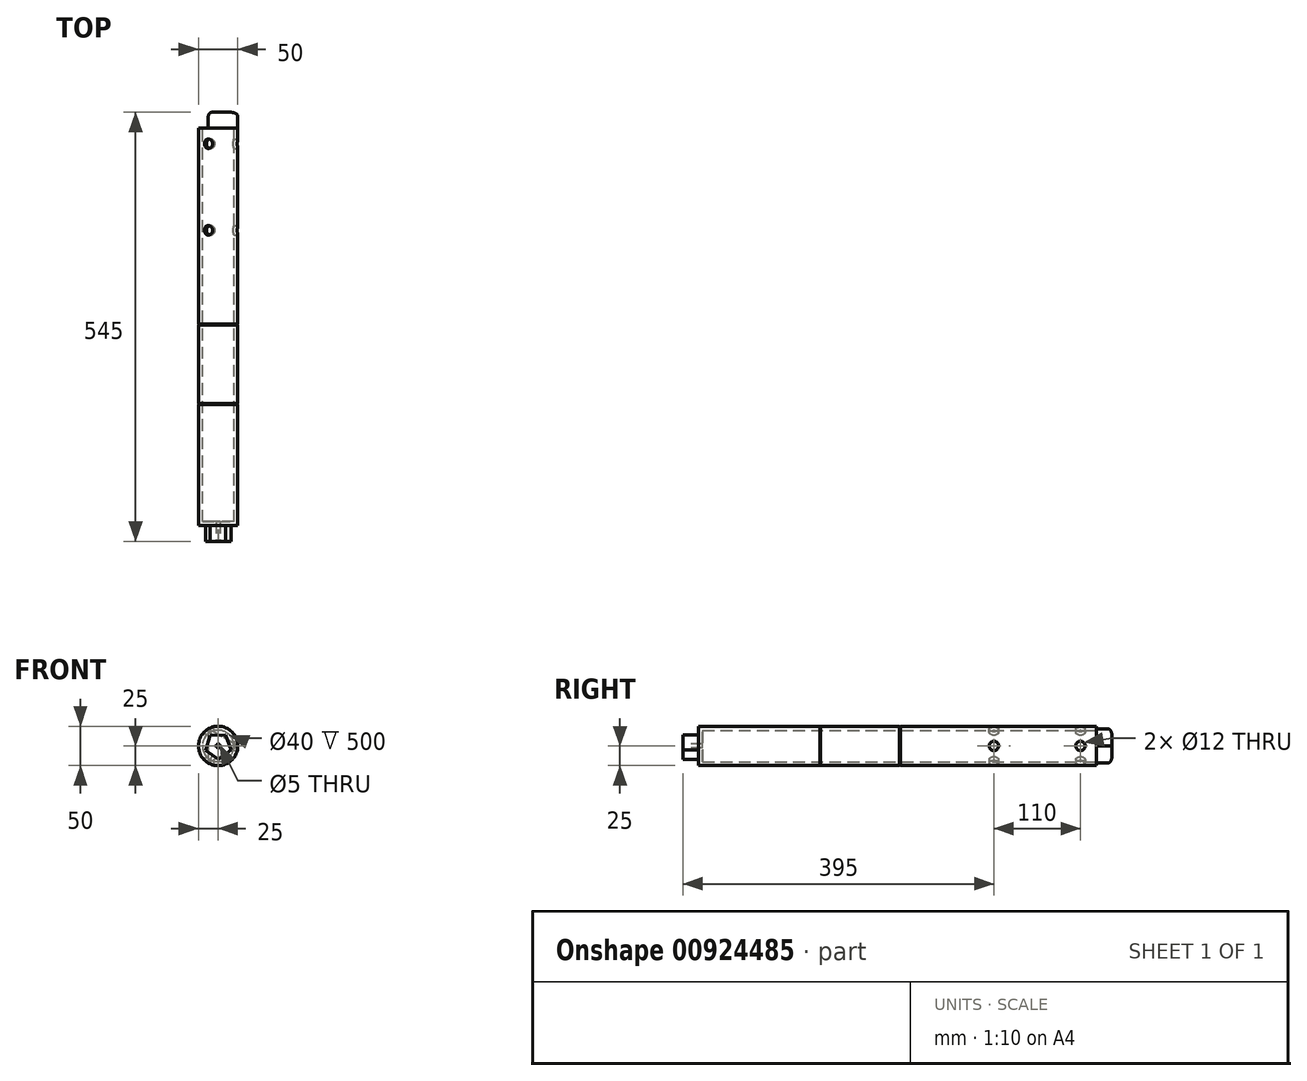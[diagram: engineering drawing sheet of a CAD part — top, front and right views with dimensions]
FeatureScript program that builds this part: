
annotation { "Feature Type Name" : "Feature", "Feature Type Description" : "" }
export const myFeature = defineFeature(function(context is Context, id is Id, definition is map)
    precondition{}
    {
        {
            var Q0;
            Q0=qCreatedBy(makeId("Front.planeOp"),FACE);
            var sketch = newSketch(context, id + "F0", { "sketchPlane" : qUnion([Q0])});
            skCircle(sketch, "E0", {"center": v(0, 0) * mm, "radius": 25 * mm});
            skCircle(sketch, "E1", {"center": v(0, 0) * mm, "radius": 20 * mm});
            skSolve(sketch);
        }
        {
            var Q0;
            Q0=makeQuery(id+"F0.imprint","IMPRINT",FACE,{"disambiguationData":[TD([[makeQuery(id+"F0.imprint","IMPRINT",EDGE,{"derivedFrom":sQuery(id+"F0.wireOp",EDGE,"E0")}),1.0]])]});
            extrude(context, id + "F1", {"entities" : qUnion([Q0]), "depth" : 500 * mm, "offsetDistance" : 25 * mm});
        }
        {
            var Q0;
            Q0=makeQuery(id+"F1.opExtrude","CAP_FACE",FACE,{"disambiguationData":[OSD([sQuery(id+"F0.wireOp",EDGE,"E0"),sQuery(id+"F0.wireOp",EDGE,"E1")])],"isStart":false});
            var sketch = newSketch(context, id + "F2", { "sketchPlane" : qUnion([Q0])});
            skCircle(sketch, "E2", {"center": v(0, 0) * mm, "radius": 25 * mm});
            skSolve(sketch);
        }
        {
            var Q0;
            Q0=qSketchRegion(id+"F2",true);
            extrude(context, id + "F3", {"entities" : qUnion([Q0]), "operationType" : NewBodyOperationType.ADD, "depth" : 5 * mm, "offsetDistance" : 25 * mm});
        }
        {
            var Q0;
            Q0=makeQuery(id+"F3.opExtrude","CAP_FACE",FACE,{"disambiguationData":[OSD([sQuery(id+"F2.wireOp",EDGE,"E2")])],"isStart":false});
            var sketch = newSketch(context, id + "F4", { "sketchPlane" : qUnion([Q0])});
            skCircle(sketch, "E3.cCircle", {"center": v(0, 0) * mm, "radius": 13.77 * mm, "construction": true});
            skLineSegment(sketch, "E3.0", {"start": v(0.38, -17.01) * mm, "end": v(-16.06, -5.62) * mm});
            skLineSegment(sketch, "E3.1", {"start": v(-16.06, -5.62) * mm, "end": v(-10.3, 13.54) * mm});
            skLineSegment(sketch, "E3.2", {"start": v(-10.3, 13.54) * mm, "end": v(9.7, 13.99) * mm});
            skLineSegment(sketch, "E3.3", {"start": v(9.7, 13.99) * mm, "end": v(16.3, -4.9) * mm});
            skLineSegment(sketch, "E3.4", {"start": v(16.3, -4.9) * mm, "end": v(0.38, -17.01) * mm});
            skPoint(sketch, "E3.0.midPoint", {"position": v(-7.84, -11.32) * mm});
            skSolve(sketch);
        }
        {
            var Q0;
            Q0=makeQuery(id+"F4.imprint","IMPRINT",FACE,{"disambiguationData":[TD([[makeQuery(id+"F4.imprint","IMPRINT",EDGE,{"derivedFrom":sQuery(id+"F4.wireOp",EDGE,"E3.0")}),-1.0]])]});
            extrude(context, id + "F5", {"entities" : qUnion([Q0]), "operationType" : NewBodyOperationType.ADD, "depth" : 20 * mm, "offsetDistance" : 25 * mm});
        }
        {
            var Q0;
            Q0=makeQuery(id+"F5.opExtrude","CAP_FACE",FACE,{"disambiguationData":[OSD([sQuery(id+"F4.wireOp",EDGE,"E3.0"),sQuery(id+"F4.wireOp",EDGE,"E3.1"),sQuery(id+"F4.wireOp",EDGE,"E3.2"),sQuery(id+"F4.wireOp",EDGE,"E3.3"),sQuery(id+"F4.wireOp",EDGE,"E3.4")])],"isStart":false});
            var sketch = newSketch(context, id + "F6", { "sketchPlane" : qUnion([Q0])});
            skPoint(sketch, "E4", {"position": v(0, 0) * mm});
            skSolve(sketch);
        }
        {
            var Q0;
            Q0=sQuery(id+"F6.wireOp",VERTEX,"E4");
            var Q1;
            Q1=makeQuery(id+"F1.opExtrude","SWEPT_BODY",BODY,{"disambiguationData":[OSD([sQuery(id+"F0.wireOp",EDGE,"E0"),sQuery(id+"F0.wireOp",EDGE,"E1")])]});
            hole(context, id + "F7", {"style" : HoleStyle.SIMPLE, "endStyle" : HoleEndStyle.THROUGH, "holeDiameter" : 5 * mm, "majorDiameter" : 5 * mm, "isTappedThrough" : true, "tappedDepth" : 12 * mm, "tapClearance" : 3, "locations" : qUnion([Q0]), "scope" : qUnion([Q1])});
        }
        {
            var Q0;
            Q0=qCreatedBy(makeId("Right.planeOp"),FACE);
            cPlane(context, id + "F8", {"entities" : qUnion([Q0]), "cplaneType" : CPlaneType.OFFSET, "offset" : 25 * mm, "width" : 150 * mm, "height" : 150 * mm});
        }
        {
            var Q0;
            Q0=qCreatedBy(id+"F8.planeOp",FACE);
            var sketch = newSketch(context, id + "F9", { "sketchPlane" : qUnion([Q0])});
            skPoint(sketch, "E5", {"position": v(-20, 0) * mm});
            skPoint(sketch, "E6", {"position": v(-130, 0) * mm});
            skSolve(sketch);
        }
        {
            var Q0;
            Q0=sQuery(id+"F9.wireOp",VERTEX,"E5");
            var Q1;
            Q1=sQuery(id+"F9.wireOp",VERTEX,"E6");
            var Q2;
            Q2=makeQuery(id+"F1.opExtrude","SWEPT_BODY",BODY,{"disambiguationData":[OSD([sQuery(id+"F0.wireOp",EDGE,"E0"),sQuery(id+"F0.wireOp",EDGE,"E1")])]});
            hole(context, id + "F10", {"style" : HoleStyle.SIMPLE, "endStyle" : HoleEndStyle.BLIND, "holeDiameter" : 12 * mm, "majorDiameter" : 5 * mm, "holeDepth" : 6 * mm, "isTappedThrough" : true, "tappedDepth" : 12 * mm, "tapClearance" : 3, "locations" : qUnion([Q0, Q1]), "scope" : qUnion([Q2])});
        }
        {
            var Q0;
            Q0=makeQuery(id+"F1.opExtrude","CAP_FACE",FACE,{"disambiguationData":[OSD([sQuery(id+"F0.wireOp",EDGE,"E0"),sQuery(id+"F0.wireOp",EDGE,"E1")])],"isStart":true});
            var sketch = newSketch(context, id + "F11", { "sketchPlane" : qUnion([Q0])});
            skCircle(sketch, "E7.cCircle", {"center": v(0, 0) * mm, "radius": 12.5 * mm, "construction": true});
            skLineSegment(sketch, "E7.0", {"start": v(12.5, 21.65) * mm, "end": v(12.5, -21.65) * mm});
            skLineSegment(sketch, "E7.1", {"start": v(12.5, -21.65) * mm, "end": v(-25, 0) * mm});
            skLineSegment(sketch, "E7.2", {"start": v(-25, 0) * mm, "end": v(12.5, 21.65) * mm});
            skPoint(sketch, "E7.0.midPoint", {"position": v(12.5, 0) * mm});
            skSolve(sketch);
        }
        {
            var Q0;
            Q0=qSketchRegion(id+"F11",true);
            extrude(context, id + "F12", {"entities" : qUnion([Q0]), "operationType" : NewBodyOperationType.ADD, "depth" : 20 * mm, "offsetDistance" : 25 * mm});
        }
        {
            var Q0;
            Q0=qCreatedBy(makeId("Front.planeOp"),FACE);
            cPlane(context, id + "F13", {"entities" : qUnion([Q0]), "cplaneType" : CPlaneType.OFFSET, "offset" : 25 * mm, "width" : 150 * mm, "height" : 150 * mm});
        }
        {
            var Q0;
            Q0=makeQuery(id+"F12.opExtrude","SWEPT_FACE",FACE,{"disambiguationData":[OSD([sQuery(id+"F11.wireOp",EDGE,"E7.2")])]});
            cPlane(context, id + "F14", {"entities" : qUnion([Q0]), "cplaneType" : CPlaneType.OFFSET, "offset" : 37.5 * mm, "oppositeDirection" : true, "width" : 150 * mm, "height" : 150 * mm});
        }
        {
            var Q0;
            Q0=makeQuery(id+"F12.opExtrude","SWEPT_FACE",FACE,{"disambiguationData":[OSD([sQuery(id+"F11.wireOp",EDGE,"E7.1")])]});
            cPlane(context, id + "F15", {"entities" : qUnion([Q0]), "cplaneType" : CPlaneType.OFFSET, "offset" : 37.5 * mm, "oppositeDirection" : true, "width" : 150 * mm, "height" : 150 * mm});
        }
        {
            var Q0;
            Q0=qCreatedBy(id+"F14.planeOp",FACE);
            var sketch = newSketch(context, id + "F16", { "sketchPlane" : qUnion([Q0])});
            skLineSegment(sketch, "E8", {"start": v(0, 0) * mm, "end": v(0, -597.57) * mm});
            skPoint(sketch, "E9", {"position": v(0, -20) * mm});
            skPoint(sketch, "E10", {"position": v(0, -130) * mm});
            skSolve(sketch);
        }
        {
            var Q0;
            Q0=sQuery(id+"F16.wireOp",VERTEX,"E9");
            var Q1;
            Q1=sQuery(id+"F16.wireOp",VERTEX,"E10");
            var Q2;
            Q2=makeQuery(id+"F1.opExtrude","SWEPT_BODY",BODY,{"disambiguationData":[OSD([sQuery(id+"F0.wireOp",EDGE,"E0"),sQuery(id+"F0.wireOp",EDGE,"E1")])]});
            hole(context, id + "F17", {"style" : HoleStyle.SIMPLE, "endStyle" : HoleEndStyle.BLIND, "oppositeDirection" : true, "holeDiameter" : 12 * mm, "majorDiameter" : 5 * mm, "holeDepth" : 6 * mm, "isTappedThrough" : true, "tappedDepth" : 12 * mm, "tapClearance" : 3, "locations" : qUnion([Q0, Q1]), "scope" : qUnion([Q2])});
        }
        {
            var Q0;
            Q0=qCreatedBy(id+"F15.planeOp",FACE);
            var sketch = newSketch(context, id + "F18", { "sketchPlane" : qUnion([Q0])});
            skLineSegment(sketch, "E11", {"start": v(0, 0) * mm, "end": v(0, 1140.88) * mm});
            skPoint(sketch, "E12", {"position": v(0, 20) * mm});
            skPoint(sketch, "E13", {"position": v(0, 130) * mm});
            skSolve(sketch);
        }
        {
            var Q0;
            Q0=sQuery(id+"F18.wireOp",VERTEX,"E12");
            var Q1;
            Q1=sQuery(id+"F18.wireOp",VERTEX,"E13");
            var Q2;
            Q2=makeQuery(id+"F1.opExtrude","SWEPT_BODY",BODY,{"disambiguationData":[OSD([sQuery(id+"F0.wireOp",EDGE,"E0"),sQuery(id+"F0.wireOp",EDGE,"E1")])]});
            hole(context, id + "F19", {"style" : HoleStyle.SIMPLE, "endStyle" : HoleEndStyle.BLIND, "oppositeDirection" : true, "holeDiameter" : 12 * mm, "majorDiameter" : 5 * mm, "holeDepth" : 6 * mm, "isTappedThrough" : true, "tappedDepth" : 12 * mm, "tapClearance" : 3, "locations" : qUnion([Q0, Q1]), "scope" : qUnion([Q2])});
        }
        {
            var Q0;
            Q0=makeQuery(id+"F12.opExtrude","CAP_EDGE",EDGE,{"disambiguationData":[OSD([sQuery(id+"F11.wireOp",EDGE,"E7.2")])],"isStart":false});
            var Q1;
            Q1=makeQuery(id+"F12.opExtrude","CAP_EDGE",EDGE,{"disambiguationData":[OSD([sQuery(id+"F11.wireOp",EDGE,"E7.0")])],"isStart":false});
            var Q2;
            Q2=makeQuery(id+"F12.opExtrude","CAP_EDGE",EDGE,{"disambiguationData":[OSD([sQuery(id+"F11.wireOp",EDGE,"E7.1")])],"isStart":false});
            fillet(context, id + "F20", {"entities" : qUnion([Q0, Q1, Q2]), "radius" : 5 * mm, "tangentPropagation" : true, "allowEdgeOverflow" : false});
        }
        {
            var Q0;
            Q0=qCreatedBy(makeId("Front.planeOp"),FACE);
            cPlane(context, id + "F21", {"entities" : qUnion([Q0]), "cplaneType" : CPlaneType.OFFSET, "offset" : 250 * mm, "width" : 150 * mm, "height" : 150 * mm});
        }
        {
            var Q0;
            Q0=qCreatedBy(id+"F21.planeOp",FACE);
            var sketch = newSketch(context, id + "F22", { "sketchPlane" : qUnion([Q0])});
            skCircle(sketch, "E14", {"center": v(0, 0) * mm, "radius": 24 * mm});
            skCircle(sketch, "E15", {"center": v(0, 0) * mm, "radius": 25 * mm});
            skSolve(sketch);
        }
        {
            var Q0;
            Q0=qSketchRegion(id+"F22",true);
            extrude(context, id + "F23", {"entities" : qUnion([Q0]), "operationType" : NewBodyOperationType.REMOVE, "oppositeDirection" : true, "depth" : 1 * mm, "offsetDistance" : 25 * mm});
        }
        {
            var Q0;
            Q0=qCreatedBy(id+"F21.planeOp",FACE);
            cPlane(context, id + "F24", {"entities" : qUnion([Q0]), "cplaneType" : CPlaneType.OFFSET, "offset" : 100 * mm, "width" : 150 * mm, "height" : 150 * mm});
        }
        {
            var Q0;
            Q0=qCreatedBy(id+"F24.planeOp",FACE);
            var sketch = newSketch(context, id + "F25", { "sketchPlane" : qUnion([Q0])});
            skCircle(sketch, "E16", {"center": v(0, 0) * mm, "radius": 24 * mm});
            skCircle(sketch, "E17", {"center": v(0, 0) * mm, "radius": 25 * mm});
            skSolve(sketch);
        }
        {
            var Q0;
            Q0=qSketchRegion(id+"F25",true);
            extrude(context, id + "F26", {"entities" : qUnion([Q0]), "operationType" : NewBodyOperationType.REMOVE, "depth" : 1 * mm, "offsetDistance" : 25 * mm});
        }
    });
